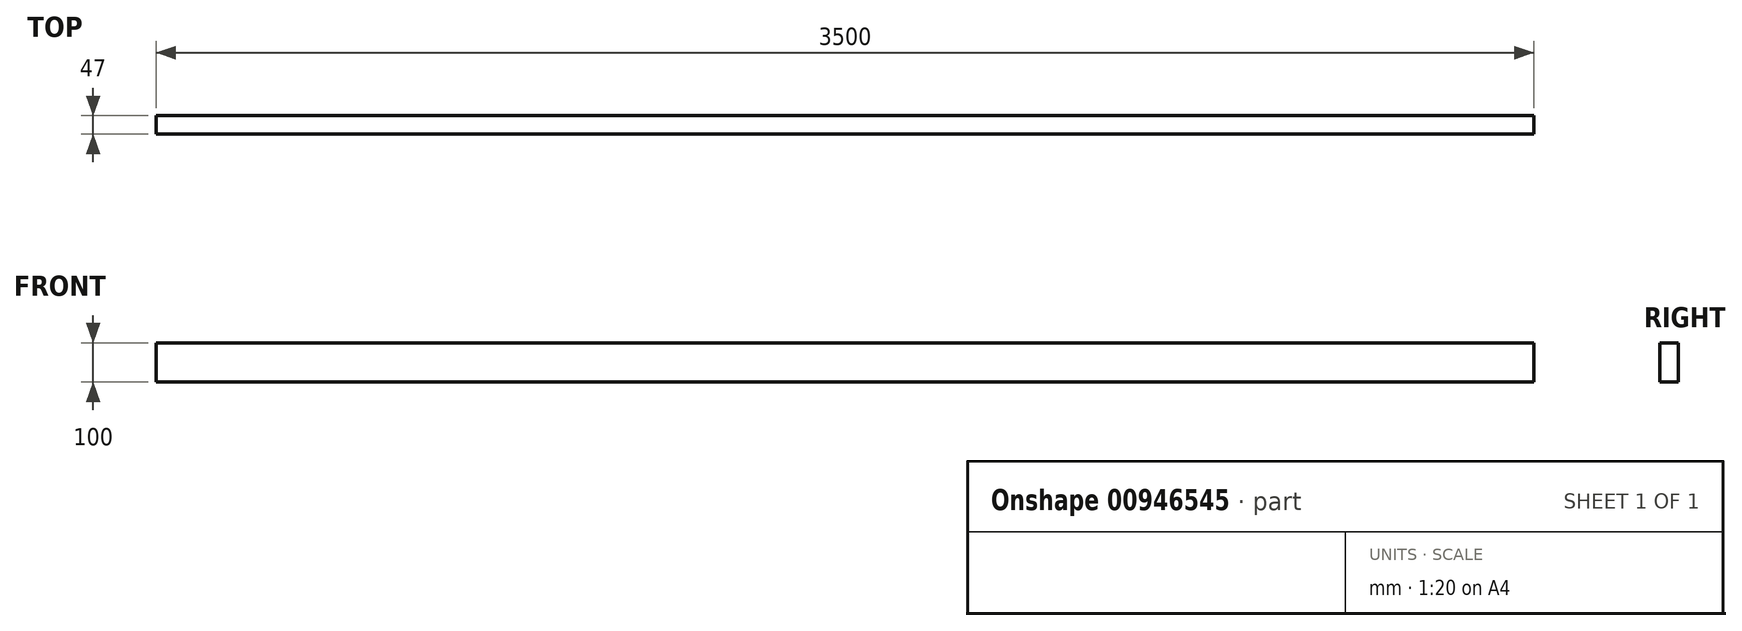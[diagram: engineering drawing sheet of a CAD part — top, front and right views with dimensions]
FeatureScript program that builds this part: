
annotation { "Feature Type Name" : "Feature", "Feature Type Description" : "" }
export const myFeature = defineFeature(function(context is Context, id is Id, definition is map)
    precondition{}
    {
        {
            var Q0;
            Q0=qCreatedBy(makeId("Right.planeOp"),FACE);
            var sketch = newSketch(context, id + "F0", { "sketchPlane" : qUnion([Q0])});
            skLineSegment(sketch, "E0.bottom", {"start": v(0, 0) * mm, "end": v(-47, 0) * mm});
            skLineSegment(sketch, "E0.top", {"start": v(0, 100) * mm, "end": v(-47, 100) * mm});
            skLineSegment(sketch, "E0.left", {"start": v(0, 0) * mm, "end": v(0, 100) * mm});
            skLineSegment(sketch, "E0.right", {"start": v(-47, 0) * mm, "end": v(-47, 100) * mm});
            skSolve(sketch);
        }
        {
            var Q0;
            Q0 = qSketchRegion(id + "F0", true);
            extrude(context, id + "F1", {"entities" : qUnion([Q0]), "depth" : 3500 * mm, "offsetDistance" : 25 * mm});
        }
    });
